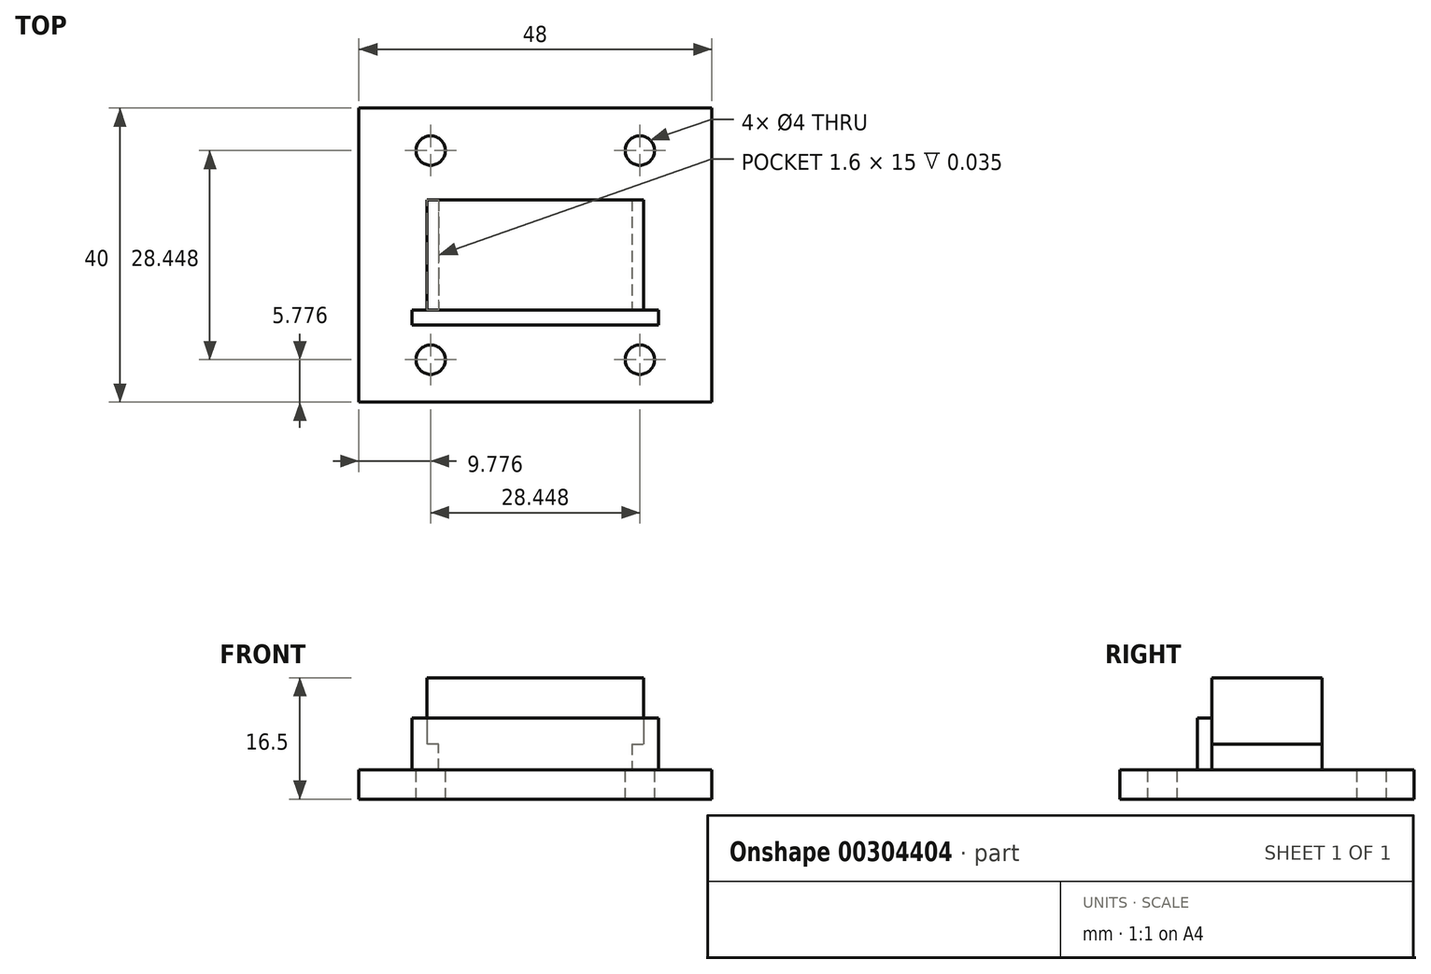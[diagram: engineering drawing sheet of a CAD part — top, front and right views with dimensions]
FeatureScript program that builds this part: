
annotation { "Feature Type Name" : "Feature", "Feature Type Description" : "" }
export const myFeature = defineFeature(function(context is Context, id is Id, definition is map)
    precondition{}
    {
        {
            var Q0;
            Q0=qCreatedBy(makeId("Top.planeOp"),FACE);
            var sketch = newSketch(context, id + "F0", { "sketchPlane" : qUnion([Q0])});
            skLineSegment(sketch, "E0.bottom", {"start": v(24, 20) * mm, "end": v(-24, 20) * mm});
            skLineSegment(sketch, "E0.top", {"start": v(24, -20) * mm, "end": v(-24, -20) * mm});
            skLineSegment(sketch, "E0.left", {"start": v(24, 20) * mm, "end": v(24, -20) * mm});
            skLineSegment(sketch, "E0.right", {"start": v(-24, 20) * mm, "end": v(-24, -20) * mm});
            skPoint(sketch, "E0.middle", {"position": v(0, 0) * mm});
            skSolve(sketch);
        }
        {
            var Q0;
            Q0=makeQuery(id+"F0.imprint","IMPRINT",FACE,{"disambiguationData":[TD([[makeQuery(id+"F0.imprint","IMPRINT",EDGE,{"derivedFrom":sQuery(id+"F0.wireOp",EDGE,"E0.bottom")}),1.0]])]});
            extrude(context, id + "F1", {"entities" : qUnion([Q0]), "depth" : 4 * mm});
        }
        {
            var Q0;
            Q0=makeQuery(id+"F1.opExtrude","CAP_FACE",FACE,{"disambiguationData":[OSD([sQuery(id+"F0.wireOp",EDGE,"E0.bottom"),sQuery(id+"F0.wireOp",EDGE,"E0.top"),sQuery(id+"F0.wireOp",EDGE,"E0.left"),sQuery(id+"F0.wireOp",EDGE,"E0.right")])],"isStart":false});
            var sketch = newSketch(context, id + "F2", { "sketchPlane" : qUnion([Q0])});
            skCircle(sketch, "E1", {"center": v(-14.22, 14.22) * mm, "radius": 2 * mm});
            skCircle(sketch, "E2.MirrorC", {"center": v(14.22, 14.22) * mm, "radius": 2 * mm});
            skCircle(sketch, "E3.MirrorC", {"center": v(-14.22, -14.22) * mm, "radius": 2 * mm});
            skCircle(sketch, "E4.MirrorC", {"center": v(14.22, -14.22) * mm, "radius": 2 * mm});
            skSolve(sketch);
        }
        {
            var Q0;
            Q0 = qSketchRegion(id + "F2", true);
            extrude(context, id + "F3", {"entities" : qUnion([Q0]), "operationType" : NewBodyOperationType.REMOVE, "endBound" : BoundingType.THROUGH_ALL, "oppositeDirection" : true, "depth" : 25 * mm});
        }
        {
            var Q0;
            Q0=makeQuery(id+"F1.opExtrude","CAP_FACE",FACE,{"disambiguationData":[OSD([sQuery(id+"F0.wireOp",EDGE,"E0.bottom"),sQuery(id+"F0.wireOp",EDGE,"E0.top"),sQuery(id+"F0.wireOp",EDGE,"E0.left"),sQuery(id+"F0.wireOp",EDGE,"E0.right")])],"isStart":false});
            var sketch = newSketch(context, id + "F4", { "sketchPlane" : qUnion([Q0])});
            skLineSegment(sketch, "E5.bottom", {"start": v(14.75, 7.5) * mm, "end": v(-14.75, 7.5) * mm});
            skLineSegment(sketch, "E5.top", {"start": v(14.75, -7.5) * mm, "end": v(-14.75, -7.5) * mm});
            skLineSegment(sketch, "E5.left", {"start": v(14.75, 7.5) * mm, "end": v(14.75, -7.5) * mm});
            skLineSegment(sketch, "E5.right", {"start": v(-14.75, 7.5) * mm, "end": v(-14.75, -7.5) * mm});
            skPoint(sketch, "E5.middle", {"position": v(0, 0) * mm});
            skSolve(sketch);
        }
        {
            var Q0;
            Q0 = qSketchRegion(id + "F4", true);
            extrude(context, id + "F5", {"entities" : qUnion([Q0]), "operationType" : NewBodyOperationType.ADD, "depth" : 12.5 * mm});
        }
        {
            var Q0;
            Q0=makeQuery(id+"F5.opExtrude","SWEPT_FACE",FACE,{"disambiguationData":[OSD([sQuery(id+"F4.wireOp",EDGE,"E5.right")])]});
            var sketch = newSketch(context, id + "F6", { "sketchPlane" : qUnion([Q0])});
            skLineSegment(sketch, "E6.bottom", {"start": v(-7.5, 3.97) * mm, "end": v(7.5, 3.97) * mm});
            skLineSegment(sketch, "E6.left", {"start": v(-7.5, 3.97) * mm, "end": v(-7.5, 7.5) * mm});
            skLineSegment(sketch, "E6.right", {"start": v(7.5, 3.97) * mm, "end": v(7.5, 7.5) * mm});
            skLineSegment(sketch, "E7.bottom", {"start": v(-7.5, 4) * mm, "end": v(7.5, 4) * mm});
            skLineSegment(sketch, "E7.top", {"start": v(-7.5, 7.5) * mm, "end": v(7.5, 7.5) * mm});
            skLineSegment(sketch, "E7.left", {"start": v(-7.5, 4) * mm, "end": v(-7.5, 7.5) * mm});
            skLineSegment(sketch, "E7.right", {"start": v(7.5, 4) * mm, "end": v(7.5, 7.5) * mm});
            skSolve(sketch);
        }
        {
            var Q0;
            Q0 = qSketchRegion(id + "F6", true);
            extrude(context, id + "F7", {"entities" : qUnion([Q0]), "operationType" : NewBodyOperationType.REMOVE, "oppositeDirection" : true, "depth" : 1.6 * mm});
        }
        {
            var Q0;
            Q0=makeQuery(id+"F5.opExtrude","SWEPT_FACE",FACE,{"disambiguationData":[OSD([sQuery(id+"F4.wireOp",EDGE,"E5.left")])]});
            var sketch = newSketch(context, id + "F8", { "sketchPlane" : qUnion([Q0])});
            skLineSegment(sketch, "E8.bottom", {"start": v(-7.5, 4) * mm, "end": v(7.5, 4) * mm});
            skLineSegment(sketch, "E8.top", {"start": v(-7.5, 7.5) * mm, "end": v(7.5, 7.5) * mm});
            skLineSegment(sketch, "E8.left", {"start": v(-7.5, 4) * mm, "end": v(-7.5, 7.5) * mm});
            skLineSegment(sketch, "E8.right", {"start": v(7.5, 4) * mm, "end": v(7.5, 7.5) * mm});
            skSolve(sketch);
        }
        {
            var Q0;
            Q0 = qSketchRegion(id + "F8", true);
            extrude(context, id + "F9", {"entities" : qUnion([Q0]), "operationType" : NewBodyOperationType.REMOVE, "oppositeDirection" : true, "depth" : 1.6 * mm});
        }
        {
            var Q0;
            Q0 = qSketchRegion(id + "F6", true);
            extrude(context, id + "F10", {"entities" : qUnion([Q0]), "operationType" : NewBodyOperationType.REMOVE, "oppositeDirection" : true, "depth" : 1.6 * mm});
        }
        {
            var Q0;
            Q0=makeQuery(id+"F5.opExtrude","SWEPT_FACE",FACE,{"disambiguationData":[OSD([sQuery(id+"F4.wireOp",EDGE,"E5.top")])]});
            var sketch = newSketch(context, id + "F11", { "sketchPlane" : qUnion([Q0])});
            skLineSegment(sketch, "E9.bottom", {"start": v(-16.75, 4) * mm, "end": v(16.75, 4) * mm});
            skLineSegment(sketch, "E9.top", {"start": v(-16.75, 11) * mm, "end": v(16.75, 11) * mm});
            skLineSegment(sketch, "E9.left", {"start": v(-16.75, 4) * mm, "end": v(-16.75, 11) * mm});
            skLineSegment(sketch, "E9.right", {"start": v(16.75, 4) * mm, "end": v(16.75, 11) * mm});
            skPoint(sketch, "E9.middle", {"position": v(0, 7.5) * mm});
            skPoint(sketch, "E9.middle.positionSnap0", {"position": v(0, 4) * mm});
            skPoint(sketch, "E9.centerSnap0", {"position": v(0, 4) * mm});
            skSolve(sketch);
        }
        {
            var Q0;
            Q0 = qSketchRegion(id + "F11", true);
            extrude(context, id + "F12", {"entities" : qUnion([Q0]), "operationType" : NewBodyOperationType.ADD, "depth" : 2 * mm});
        }
    });
